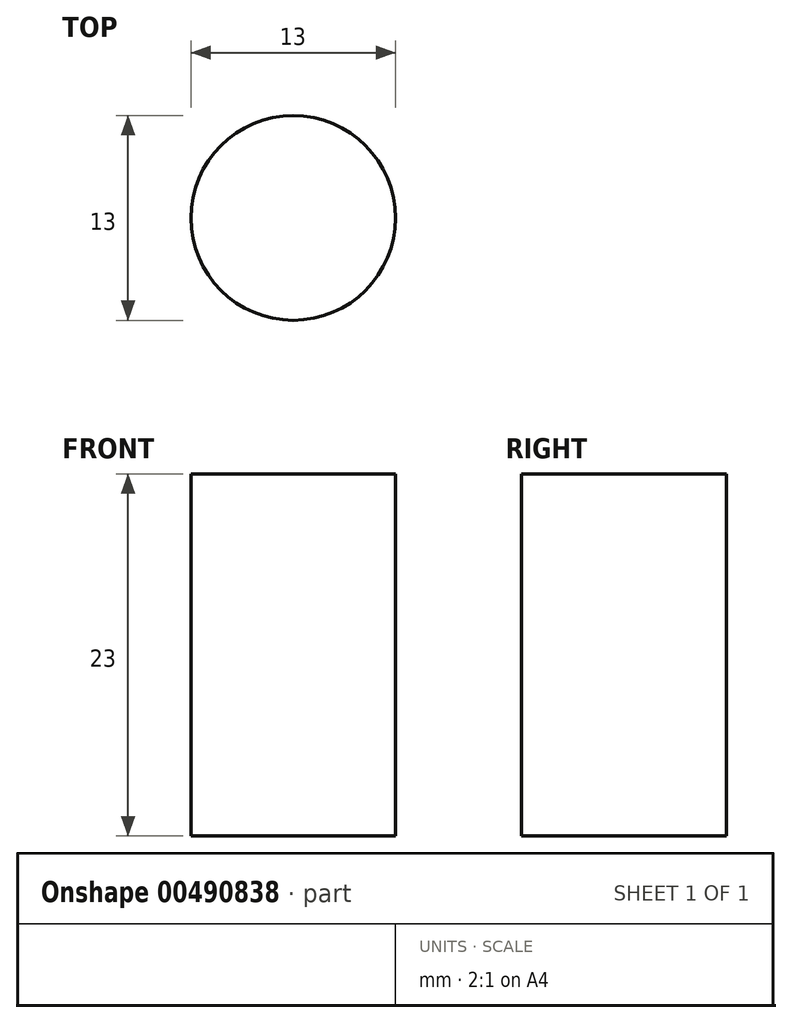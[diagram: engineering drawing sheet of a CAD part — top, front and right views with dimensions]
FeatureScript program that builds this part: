
annotation { "Feature Type Name" : "Feature", "Feature Type Description" : "" }
export const myFeature = defineFeature(function(context is Context, id is Id, definition is map)
    precondition{}
    {
        {
            var Q0;
            Q0=qCreatedBy(makeId("Top.planeOp"),FACE);
            var sketch = newSketch(context, id + "F0", { "sketchPlane" : qUnion([Q0])});
            skCircle(sketch, "E0", {"center": v(0, 0) * mm, "radius": 6.5 * mm});
            skSolve(sketch);
        }
        {
            var Q0;
            Q0=makeQuery(id+"F0.imprint","IMPRINT",FACE,{"disambiguationData":[TD([[makeQuery(id+"F0.imprint","IMPRINT",EDGE,{"derivedFrom":sQuery(id+"F0.wireOp",EDGE,"E0")}),1.0]])]});
            extrude(context, id + "F1", {"entities" : qUnion([Q0]), "depth" : 23 * mm, "offsetDistance" : 25 * mm});
        }
    });
